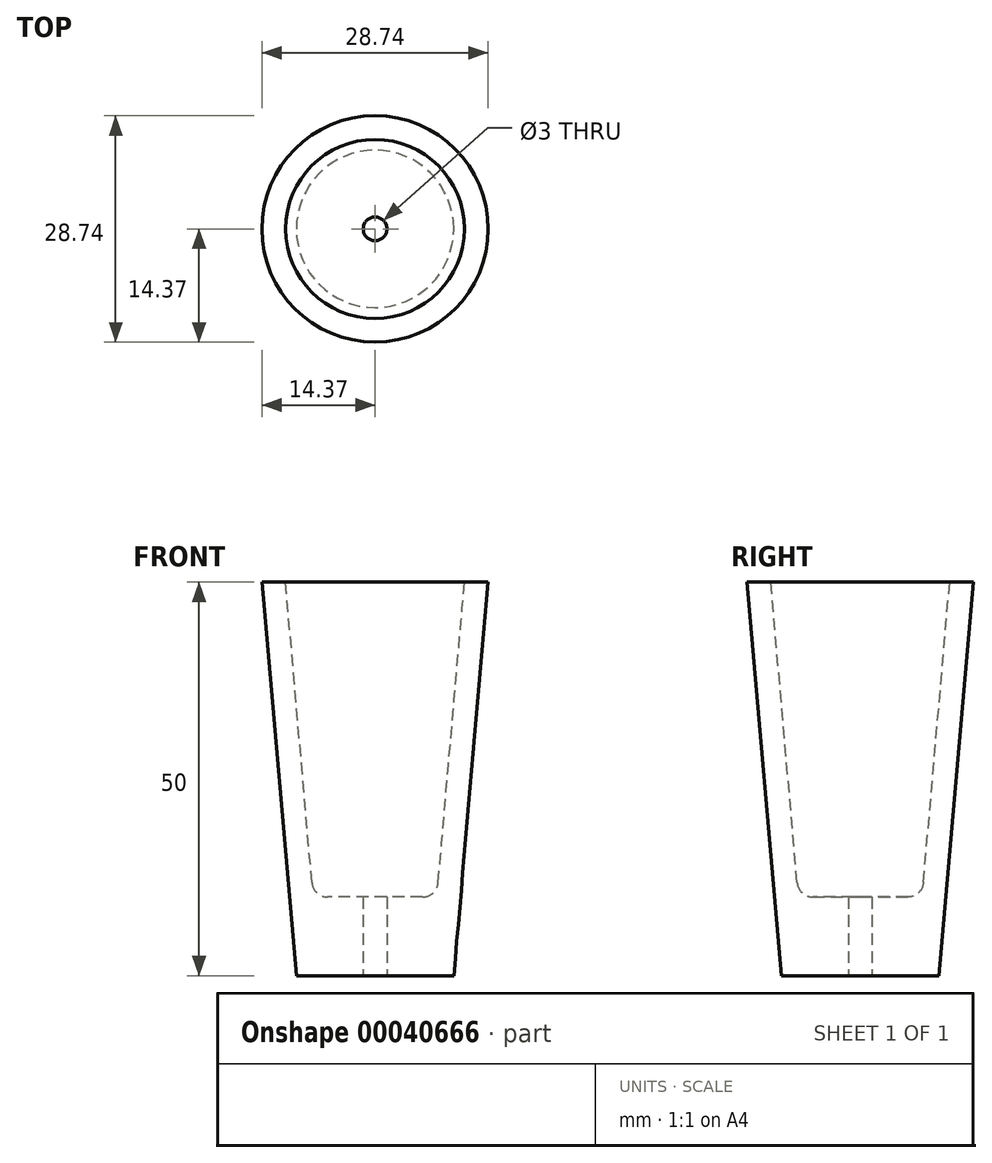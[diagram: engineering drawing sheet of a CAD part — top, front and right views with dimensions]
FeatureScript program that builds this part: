
annotation { "Feature Type Name" : "Feature", "Feature Type Description" : "" }
export const myFeature = defineFeature(function(context is Context, id is Id, definition is map)
    precondition{}
    {
        {
            var Q0;
            Q0=qCreatedBy(makeId("Top.planeOp"),FACE);
            var sketch = newSketch(context, id + "F0", { "sketchPlane" : qUnion([Q0])});
            skCircle(sketch, "E0", {"center": v(0, 0) * mm, "radius": 10 * mm});
            skSolve(sketch);
        }
        {
            var Q0;
            Q0 = qSketchRegion(id + "F0", true);
            extrude(context, id + "F1", {"entities" : qUnion([Q0]), "depth" : 50 * mm, "hasDraft" : true, "draftAngle" : 5 * degree});
        }
        {
            var Q0;
            Q0=makeQuery(id+"F1.opExtrude","CAP_FACE",FACE,{"disambiguationData":[OSD([sQuery(id+"F0.wireOp",EDGE,"E0")])],"isStart":false});
            shell(context, id + "F2", {"entities" : qUnion([Q0]), "thickness" : 3 * mm});
        }
        {
            var Q0;
            Q0 = qSketchRegion(id + "F0", true);
            extrude(context, id + "F3", {"entities" : qUnion([Q0]), "operationType" : NewBodyOperationType.ADD, "depth" : 10 * mm});
        }
        {
            var Q0;
            Q0=sQuery(id+"F0.wireOp",VERTEX,"E0.center");
            var Q1;
            Q1=makeQuery(id+"F1.opExtrude","SWEPT_BODY",BODY,{"disambiguationData":[OSD([sQuery(id+"F0.wireOp",EDGE,"E0")])]});
            hole(context, id + "F4", {"style" : HoleStyle.SIMPLE, "holeDiameter" : 3 * mm, "endStyle" : HoleEndStyle.THROUGH, "oppositeDirection" : true, "locations" : qUnion([Q0]), "scope" : qUnion([Q1])});
        }
        {
            var Q0;
            {var subQ0=sQuery(id+"F0.wireOp",EDGE,"E0");Q0=makeQuery(id+"F3.boolean.opBoolean","INTERSECT",EDGE,{"derivedFrom":[makeQuery(id+"F2.opShell","OFFSET_FACE",FACE,{"disambiguationData":[OSD([subQ0]),TDD([makeQuery(id+"F1.opExtrude","SWEPT_FACE",FACE,{"disambiguationData":[OSD([subQ0])]})])]}),makeQuery(id+"F3.opExtrude","CAP_FACE",FACE,{"disambiguationData":[OSD([subQ0])],"isStart":false})]});}
            fillet(context, id + "F5", {"entities" : qUnion([Q0]), "radius" : 2 * mm, "tangentPropagation" : true, "allowEdgeOverflow" : false});
        }
    });
